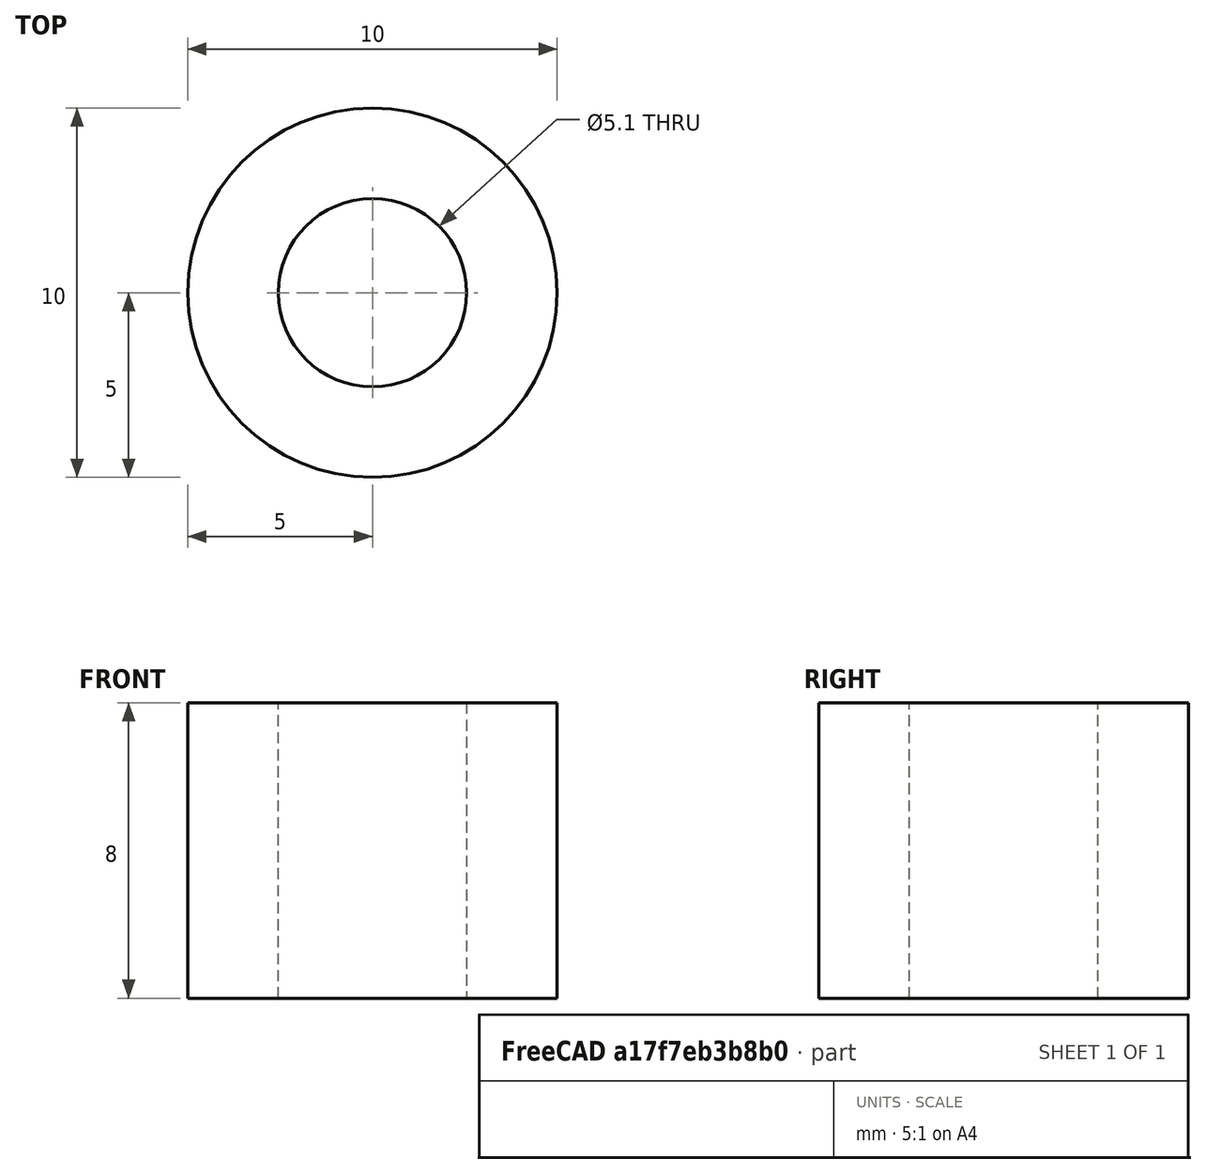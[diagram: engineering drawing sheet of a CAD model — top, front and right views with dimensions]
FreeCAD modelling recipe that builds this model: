
FCSTD DOCUMENT  (FreeCAD 0.17R10423 (Git))
Label: spacer_long
License: All rights reserved
LicenseURL: http://en.wikipedia.org/wiki/All_rights_reserved
objects: Part::Cylinder×1, PartDesign::ShapeBinder×1, Sketcher::SketchObject×1, PartDesign::Pocket×1, PartDesign::Body×1
note: 6 computed .brp shape members not serialized (recipe doc carries the construction recipe); baked Part::Feature solids carry a one-line shape summary decoded from their .brp

FEATURE [Part::Cylinder] Cylinder
  Angle = 360
  AttacherType = Attacher::AttachEngine3D
  Height = 8
  Placement = pos=(-26,22,0) rot=(0,0,1;0rad)
  Radius = 5
FEATURE [PartDesign::ShapeBinder] CopyCylinder
  Placement = pos=(-26,22,0) rot=(0,0,1;0rad)
FEATURE [Sketcher::SketchObject] Sketch002
  MapMode = 5
  Placement = pos=(-26,22,11) rot=(0,0,1;0rad)
  Support = -> [CopyCylinder]
  sketch-geometry (1):
    g0: Circle CenterX=0 CenterY=0 CenterZ=0 NormalX=0 NormalY=0 NormalZ=1 Radius=2.55
  constraints (2):
    c: Coincident(g0,g-1)
    c: Radius(g0) = 2.55
FEATURE [PartDesign::Pocket] Pocket001
  BaseFeature = -> Cylinder
  Length = 5
  Placement = pos=(-26,22,0) rot=(0,0,1;0rad)
  Profile = -> Sketch002
  Type = 1
FEATURE [PartDesign::Body] Body001  label="spacer_long"
  BaseFeature = -> Cylinder
  Group = -> [CopyCylinder,Sketch002,Pocket001]
  Origin = -> Body001Origin
  Tip = -> Pocket001
